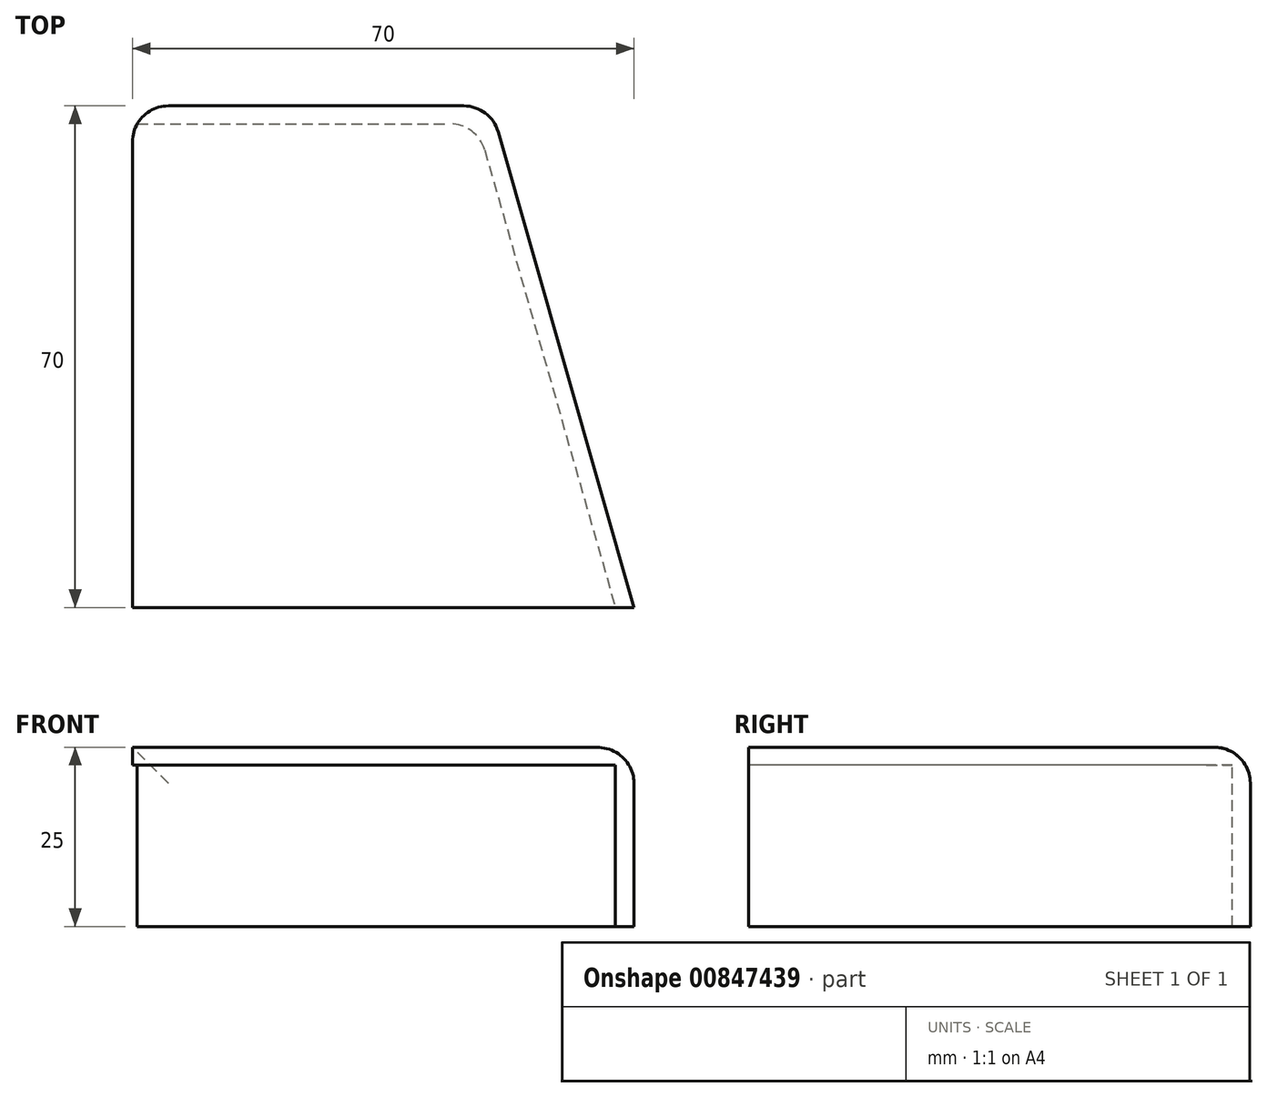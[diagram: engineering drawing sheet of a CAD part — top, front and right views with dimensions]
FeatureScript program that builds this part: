
annotation { "Feature Type Name" : "Feature", "Feature Type Description" : "" }
export const myFeature = defineFeature(function(context is Context, id is Id, definition is map)
    precondition{}
    {
        {
            var Q0;
            Q0=qCreatedBy(makeId("Top.planeOp"),FACE);
            var sketch = newSketch(context, id + "F0", { "sketchPlane" : qUnion([Q0])});
            skLineSegment(sketch, "E0", {"start": v(-37.79, 29.67) * mm, "end": v(-37.79, -40.33) * mm});
            skLineSegment(sketch, "E1", {"start": v(-37.79, -40.33) * mm, "end": v(32.21, -40.33) * mm});
            skLineSegment(sketch, "E2", {"start": v(-37.79, 29.67) * mm, "end": v(12.21, 29.67) * mm});
            skLineSegment(sketch, "E3", {"start": v(12.21, 29.67) * mm, "end": v(32.21, -40.33) * mm});
            skSolve(sketch);
        }
        {
            var Q0;
            Q0=makeQuery(id+"F0.imprint","IMPRINT",FACE,{"disambiguationData":[TD([[makeQuery(id+"F0.imprint","IMPRINT",EDGE,{"derivedFrom":sQuery(id+"F0.wireOp",EDGE,"E0")}),1.0]])]});
            extrude(context, id + "F1", {"entities" : qUnion([Q0]), "depth" : 25 * mm, "offsetDistance" : 25 * mm});
        }
        {
            var Q0;
            Q0=makeQuery(id+"F1.opExtrude","SWEPT_FACE",FACE,{"disambiguationData":[OSD([sQuery(id+"F0.wireOp",EDGE,"E0")])]});
            var Q1;
            Q1=makeQuery(id+"F1.opExtrude","CAP_FACE",FACE,{"disambiguationData":[OSD([sQuery(id+"F0.wireOp",EDGE,"E0"),sQuery(id+"F0.wireOp",EDGE,"E1"),sQuery(id+"F0.wireOp",EDGE,"E2"),sQuery(id+"F0.wireOp",EDGE,"E3")])],"isStart":true});
            var Q2;
            Q2=makeQuery(id+"F1.opExtrude","SWEPT_FACE",FACE,{"disambiguationData":[OSD([sQuery(id+"F0.wireOp",EDGE,"E1")])]});
            shell(context, id + "F2", {"entities" : qUnion([Q0, Q1, Q2]), "thickness" : 2.5 * mm});
        }
        {
            var Q0;
            Q0=makeQuery(id+"F1.opExtrude","SWEPT_EDGE",EDGE,{"disambiguationData":[OSD([sQuery(id+"F0.wireOp",EDGE,"E2"),sQuery(id+"F0.wireOp",EDGE,"E3")])]});
            var Q1;
            Q1=makeQuery(id+"F2.opShell","OFFSET_EDGE",EDGE,{"disambiguationData":[OSD([sQuery(id+"F0.wireOp",EDGE,"E2"),sQuery(id+"F0.wireOp",EDGE,"E3")])]});
            var Q2;
            Q2=makeQuery(id+"F1.opExtrude","CAP_EDGE",EDGE,{"disambiguationData":[OSD([sQuery(id+"F0.wireOp",EDGE,"E2")])],"isStart":false});
            var Q3;
            Q3=makeQuery(id+"F1.opExtrude","CAP_EDGE",EDGE,{"disambiguationData":[OSD([sQuery(id+"F0.wireOp",EDGE,"E3")])],"isStart":false});
            var Q4;
            Q4=makeQuery(id+"F1.opExtrude","SWEPT_EDGE",EDGE,{"disambiguationData":[OSD([sQuery(id+"F0.wireOp",EDGE,"E0"),sQuery(id+"F0.wireOp",EDGE,"E2")])]});
            fillet(context, id + "F3", {"entities" : qUnion([Q0, Q1, Q2, Q3, Q4]), "radius" : 5 * mm, "tangentPropagation" : true, "allowEdgeOverflow" : false});
        }
    });
